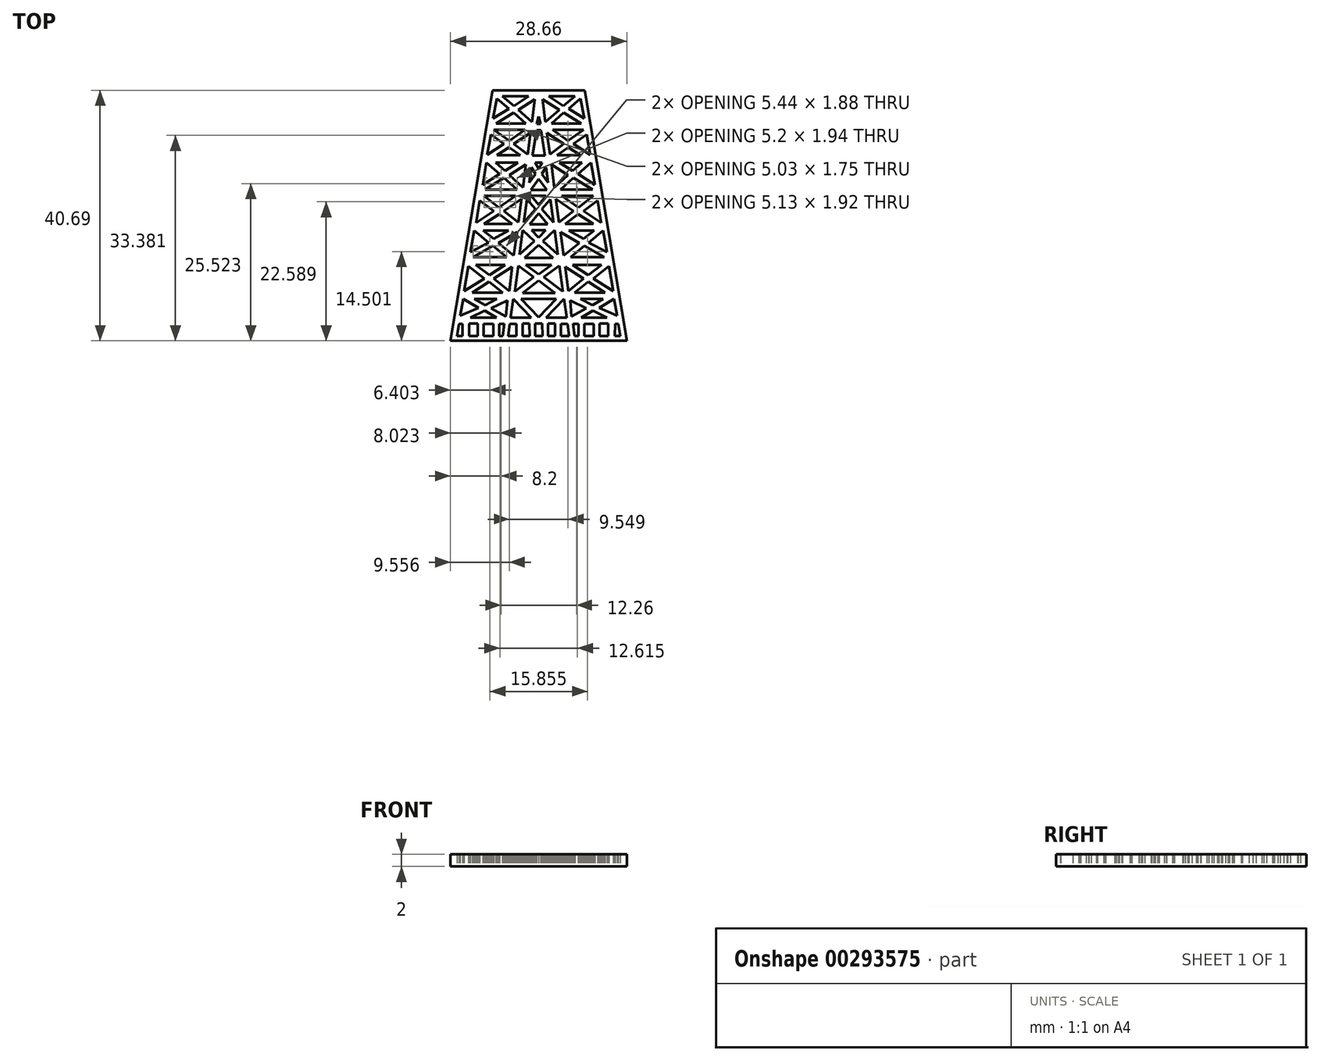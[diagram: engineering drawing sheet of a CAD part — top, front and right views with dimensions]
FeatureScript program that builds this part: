
annotation { "Feature Type Name" : "Feature", "Feature Type Description" : "" }
export const myFeature = defineFeature(function(context is Context, id is Id, definition is map)
    precondition{}
    {
        {
            var Q0;
            Q0=qCreatedBy(makeId("Top.planeOp"),FACE);
            var sketch = newSketch(context, id + "F0", { "sketchPlane" : qUnion([Q0])});
            skLineSegment(sketch, "E0", {"start": v(0, 19.4) * mm, "end": v(-7.5, 19.4) * mm});
            skLineSegment(sketch, "E1", {"start": v(-7.5, 19.4) * mm, "end": v(-14.33, -21.3) * mm});
            skLineSegment(sketch, "E2", {"start": v(-14.33, -21.3) * mm, "end": v(0, -21.3) * mm});
            skLineSegment(sketch, "E3", {"start": v(-1.53, -18.52) * mm, "end": v(-2.64, -18.52) * mm});
            skLineSegment(sketch, "E4", {"start": v(-2.64, -18.52) * mm, "end": v(-2.64, -20.5) * mm});
            skLineSegment(sketch, "E5", {"start": v(-2.64, -20.5) * mm, "end": v(-1.5, -20.5) * mm});
            skLineSegment(sketch, "E6", {"start": v(-1.5, -20.5) * mm, "end": v(-1.53, -18.52) * mm});
            skLineSegment(sketch, "E7", {"start": v(-4.7, -18.55) * mm, "end": v(-3.64, -18.55) * mm});
            skLineSegment(sketch, "E8", {"start": v(-3.64, -18.55) * mm, "end": v(-3.64, -20.51) * mm});
            skLineSegment(sketch, "E9", {"start": v(-3.64, -20.51) * mm, "end": v(-4.95, -20.51) * mm});
            skLineSegment(sketch, "E10", {"start": v(-4.95, -20.51) * mm, "end": v(-4.7, -18.55) * mm});
            skLineSegment(sketch, "E11", {"start": v(-5.57, -18.55) * mm, "end": v(-6.45, -18.55) * mm});
            skLineSegment(sketch, "E12", {"start": v(-6.45, -18.55) * mm, "end": v(-6.45, -20.51) * mm});
            skLineSegment(sketch, "E13", {"start": v(-6.45, -20.51) * mm, "end": v(-5.82, -20.51) * mm});
            skLineSegment(sketch, "E14", {"start": v(-5.82, -20.51) * mm, "end": v(-5.57, -18.55) * mm});
            skLineSegment(sketch, "E15", {"start": v(-8.95, -18.55) * mm, "end": v(-7.4, -18.55) * mm});
            skLineSegment(sketch, "E16", {"start": v(-7.4, -18.55) * mm, "end": v(-7.4, -20.53) * mm});
            skLineSegment(sketch, "E17", {"start": v(-7.4, -20.53) * mm, "end": v(-8.96, -20.53) * mm});
            skLineSegment(sketch, "E18", {"start": v(-8.96, -20.53) * mm, "end": v(-8.95, -18.55) * mm});
            skLineSegment(sketch, "E19", {"start": v(-11.3, -18.55) * mm, "end": v(-11.31, -20.52) * mm});
            skLineSegment(sketch, "E20", {"start": v(-11.31, -20.52) * mm, "end": v(-9.9, -20.52) * mm});
            skLineSegment(sketch, "E21", {"start": v(-9.9, -20.52) * mm, "end": v(-9.9, -18.52) * mm});
            skLineSegment(sketch, "E22", {"start": v(-9.9, -18.52) * mm, "end": v(-11.3, -18.51) * mm});
            skLineSegment(sketch, "E23", {"start": v(-11.3, -18.51) * mm, "end": v(-11.3, -18.55) * mm});
            skLineSegment(sketch, "E24", {"start": v(-12.42, -18.55) * mm, "end": v(-12.97, -18.55) * mm});
            skLineSegment(sketch, "E25", {"start": v(-12.97, -18.55) * mm, "end": v(-13.28, -20.51) * mm});
            skLineSegment(sketch, "E26", {"start": v(-13.28, -20.51) * mm, "end": v(-12.4, -20.52) * mm});
            skLineSegment(sketch, "E27", {"start": v(-12.4, -20.52) * mm, "end": v(-12.42, -18.55) * mm});
            skLineSegment(sketch, "E28", {"start": v(0, -18.51) * mm, "end": v(-0.6, -18.51) * mm});
            skLineSegment(sketch, "E29", {"start": v(-0.6, -18.51) * mm, "end": v(-0.6, -20.55) * mm});
            skLineSegment(sketch, "E30", {"start": v(-0.6, -20.55) * mm, "end": v(0, -20.55) * mm});
            skLineSegment(sketch, "E31", {"start": v(-11.1, -17.58) * mm, "end": v(-6.9, -17.58) * mm});
            skLineSegment(sketch, "E32", {"start": v(-6.9, -17.58) * mm, "end": v(-8.8, -16.38) * mm});
            skLineSegment(sketch, "E33", {"start": v(-8.8, -16.38) * mm, "end": v(-11.1, -17.58) * mm});
            skLineSegment(sketch, "E34", {"start": v(-12.75, -17.25) * mm, "end": v(-9.82, -15.94) * mm});
            skLineSegment(sketch, "E35", {"start": v(-9.82, -15.94) * mm, "end": v(-12.23, -14.52) * mm});
            skLineSegment(sketch, "E36", {"start": v(-12.23, -14.52) * mm, "end": v(-12.75, -17.25) * mm});
            skLineSegment(sketch, "E37", {"start": v(-10.46, -14.51) * mm, "end": v(-6.77, -14.51) * mm});
            skLineSegment(sketch, "E38", {"start": v(-6.77, -14.51) * mm, "end": v(-8.73, -15.53) * mm});
            skLineSegment(sketch, "E39", {"start": v(-8.73, -15.53) * mm, "end": v(-10.46, -14.51) * mm});
            skLineSegment(sketch, "E40", {"start": v(-5.11, -14.74) * mm, "end": v(-5.35, -17.34) * mm});
            skLineSegment(sketch, "E41", {"start": v(-5.35, -17.34) * mm, "end": v(-7.75, -16) * mm});
            skLineSegment(sketch, "E42", {"start": v(-7.75, -16) * mm, "end": v(-5.11, -14.74) * mm});
            skLineSegment(sketch, "E43", {"start": v(-10.8, -13.46) * mm, "end": v(-5.82, -13.46) * mm});
            skLineSegment(sketch, "E44", {"start": v(-5.82, -13.46) * mm, "end": v(-8.08, -11.74) * mm});
            skLineSegment(sketch, "E45", {"start": v(-8.08, -11.74) * mm, "end": v(-10.8, -13.46) * mm});
            skLineSegment(sketch, "E46", {"start": v(-12.11, -13.2) * mm, "end": v(-11.44, -9.16) * mm});
            skLineSegment(sketch, "E47", {"start": v(-11.44, -9.16) * mm, "end": v(-8.86, -11.18) * mm});
            skLineSegment(sketch, "E48", {"start": v(-8.86, -11.18) * mm, "end": v(-12.11, -13.2) * mm});
            skLineSegment(sketch, "E49", {"start": v(-4.33, -9.27) * mm, "end": v(-4.8, -13.2) * mm});
            skLineSegment(sketch, "E50", {"start": v(-4.8, -13.2) * mm, "end": v(-7.3, -11.2) * mm});
            skLineSegment(sketch, "E51", {"start": v(-7.3, -11.2) * mm, "end": v(-4.33, -9.27) * mm});
            skLineSegment(sketch, "E52", {"start": v(-5.5, -8.97) * mm, "end": v(-10.2, -8.97) * mm});
            skLineSegment(sketch, "E53", {"start": v(-10.2, -8.97) * mm, "end": v(-8.02, -10.63) * mm});
            skLineSegment(sketch, "E54", {"start": v(-8.02, -10.63) * mm, "end": v(-5.5, -8.97) * mm});
            skLineSegment(sketch, "E55", {"start": v(-6.57, -5.41) * mm, "end": v(-3.53, -3.67) * mm});
            skLineSegment(sketch, "E56", {"start": v(-3.53, -3.67) * mm, "end": v(-4.08, -7.44) * mm});
            skLineSegment(sketch, "E57", {"start": v(-4.08, -7.44) * mm, "end": v(-6.57, -5.41) * mm});
            skLineSegment(sketch, "E58", {"start": v(-7.4, -5.85) * mm, "end": v(-10.65, -7.73) * mm});
            skLineSegment(sketch, "E59", {"start": v(-10.65, -7.73) * mm, "end": v(-5.2, -7.73) * mm});
            skLineSegment(sketch, "E60", {"start": v(-5.2, -7.73) * mm, "end": v(-7.4, -5.85) * mm});
            skLineSegment(sketch, "E61", {"start": v(-11.1, -6.87) * mm, "end": v(-8.13, -5.33) * mm});
            skLineSegment(sketch, "E62", {"start": v(-8.13, -5.33) * mm, "end": v(-10.46, -3.38) * mm});
            skLineSegment(sketch, "E63", {"start": v(-10.46, -3.38) * mm, "end": v(-11.1, -6.87) * mm});
            skLineSegment(sketch, "E64", {"start": v(-9.03, -3.37) * mm, "end": v(-4.9, -3.37) * mm});
            skLineSegment(sketch, "E65", {"start": v(-4.9, -3.37) * mm, "end": v(-7.3, -4.75) * mm});
            skLineSegment(sketch, "E66", {"start": v(-7.3, -4.75) * mm, "end": v(-9.03, -3.37) * mm});
            skLineSegment(sketch, "E67", {"start": v(-8.87, -2.32) * mm, "end": v(-4.33, -2.32) * mm});
            skLineSegment(sketch, "E68", {"start": v(-4.33, -2.32) * mm, "end": v(-6.43, -0.7) * mm});
            skLineSegment(sketch, "E69", {"start": v(-6.43, -0.7) * mm, "end": v(-8.87, -2.32) * mm});
            skLineSegment(sketch, "E70", {"start": v(-10.17, -2.1) * mm, "end": v(-7.3, -0.22) * mm});
            skLineSegment(sketch, "E71", {"start": v(-7.3, -0.22) * mm, "end": v(-9.57, 1.52) * mm});
            skLineSegment(sketch, "E72", {"start": v(-9.57, 1.52) * mm, "end": v(-10.17, -2.1) * mm});
            skLineSegment(sketch, "E73", {"start": v(-8.87, 2.26) * mm, "end": v(-3.74, 2.26) * mm});
            skLineSegment(sketch, "E74", {"start": v(-3.74, 2.26) * mm, "end": v(-6.47, 0.34) * mm});
            skLineSegment(sketch, "E75", {"start": v(-6.47, 0.34) * mm, "end": v(-8.87, 2.26) * mm});
            skLineSegment(sketch, "E76", {"start": v(-2.8, 1.77) * mm, "end": v(-5.67, -0.23) * mm});
            skLineSegment(sketch, "E77", {"start": v(-5.67, -0.23) * mm, "end": v(-3.3, -2.04) * mm});
            skLineSegment(sketch, "E78", {"start": v(-3.3, -2.04) * mm, "end": v(-2.8, 1.77) * mm});
            skLineSegment(sketch, "E79", {"start": v(-7.02, 7.64) * mm, "end": v(-3.37, 7.64) * mm});
            skLineSegment(sketch, "E80", {"start": v(-3.37, 7.64) * mm, "end": v(-5.5, 6.31) * mm});
            skLineSegment(sketch, "E81", {"start": v(-5.5, 6.31) * mm, "end": v(-7.02, 7.64) * mm});
            skLineSegment(sketch, "E82", {"start": v(-8.5, 7.64) * mm, "end": v(-9.1, 4.06) * mm});
            skLineSegment(sketch, "E83", {"start": v(-9.1, 4.06) * mm, "end": v(-6.38, 5.79) * mm});
            skLineSegment(sketch, "E84", {"start": v(-6.38, 5.79) * mm, "end": v(-8.5, 7.64) * mm});
            skLineSegment(sketch, "E85", {"start": v(-5.67, 5.2) * mm, "end": v(-8.73, 3.26) * mm});
            skLineSegment(sketch, "E86", {"start": v(-8.73, 3.26) * mm, "end": v(-3.53, 3.26) * mm});
            skLineSegment(sketch, "E87", {"start": v(-3.53, 3.26) * mm, "end": v(-5.67, 5.2) * mm});
            skLineSegment(sketch, "E88", {"start": v(-2.07, 7.36) * mm, "end": v(-4.74, 5.62) * mm});
            skLineSegment(sketch, "E89", {"start": v(-4.74, 5.62) * mm, "end": v(-2.56, 3.58) * mm});
            skLineSegment(sketch, "E90", {"start": v(-2.56, 3.58) * mm, "end": v(-2.07, 7.36) * mm});
            skLineSegment(sketch, "E91", {"start": v(-4.08, 10.7) * mm, "end": v(-1.33, 12.5) * mm});
            skLineSegment(sketch, "E92", {"start": v(-1.33, 12.5) * mm, "end": v(-1.8, 9) * mm});
            skLineSegment(sketch, "E93", {"start": v(-1.8, 9) * mm, "end": v(-4.08, 10.7) * mm});
            skLineSegment(sketch, "E94", {"start": v(-2.97, 8.85) * mm, "end": v(-6.77, 8.85) * mm});
            skLineSegment(sketch, "E95", {"start": v(-6.77, 8.85) * mm, "end": v(-4.82, 10.13) * mm});
            skLineSegment(sketch, "E96", {"start": v(-4.82, 10.13) * mm, "end": v(-2.97, 8.85) * mm});
            skLineSegment(sketch, "E97", {"start": v(-8.38, 8.93) * mm, "end": v(-5.65, 10.7) * mm});
            skLineSegment(sketch, "E98", {"start": v(-5.65, 10.7) * mm, "end": v(-7.77, 12.22) * mm});
            skLineSegment(sketch, "E99", {"start": v(-7.77, 12.22) * mm, "end": v(-8.38, 8.93) * mm});
            skLineSegment(sketch, "E100", {"start": v(-7.3, 12.96) * mm, "end": v(-2.26, 12.96) * mm});
            skLineSegment(sketch, "E101", {"start": v(-2.26, 12.96) * mm, "end": v(-4.77, 11.22) * mm});
            skLineSegment(sketch, "E102", {"start": v(-4.77, 11.22) * mm, "end": v(-7.3, 12.96) * mm});
            skLineSegment(sketch, "E103", {"start": v(-6.9, 14) * mm, "end": v(-2.07, 14) * mm});
            skLineSegment(sketch, "E104", {"start": v(-2.07, 14) * mm, "end": v(-4.08, 15.77) * mm});
            skLineSegment(sketch, "E105", {"start": v(-4.08, 15.77) * mm, "end": v(-6.9, 14) * mm});
            skLineSegment(sketch, "E106", {"start": v(-0.62, 17.97) * mm, "end": v(-3.34, 16.25) * mm});
            skLineSegment(sketch, "E107", {"start": v(-3.34, 16.25) * mm, "end": v(-1.07, 14.24) * mm});
            skLineSegment(sketch, "E108", {"start": v(-1.07, 14.24) * mm, "end": v(-0.62, 17.97) * mm});
            skLineSegment(sketch, "E109", {"start": v(-7.4, 14.82) * mm, "end": v(-4.87, 16.4) * mm});
            skLineSegment(sketch, "E110", {"start": v(-4.87, 16.4) * mm, "end": v(-6.77, 18.08) * mm});
            skLineSegment(sketch, "E111", {"start": v(-6.77, 18.08) * mm, "end": v(-7.4, 14.82) * mm});
            skLineSegment(sketch, "E112", {"start": v(-5.89, 18.46) * mm, "end": v(-1.64, 18.46) * mm});
            skLineSegment(sketch, "E113", {"start": v(-1.64, 18.46) * mm, "end": v(-4.02, 16.86) * mm});
            skLineSegment(sketch, "E114", {"start": v(-4.02, 16.86) * mm, "end": v(-5.89, 18.46) * mm});
            skLineSegment(sketch, "E115", {"start": v(0, 13.92) * mm, "end": v(-0.32, 13.92) * mm});
            skLineSegment(sketch, "E116", {"start": v(-0.32, 13.92) * mm, "end": v(0, 15.18) * mm});
            skLineSegment(sketch, "E117", {"start": v(0, 8.8) * mm, "end": v(-1, 8.8) * mm});
            skLineSegment(sketch, "E118", {"start": v(-1, 8.8) * mm, "end": v(-0.35, 12.95) * mm});
            skLineSegment(sketch, "E119", {"start": v(-0.35, 12.95) * mm, "end": v(0, 12.95) * mm});
            skLineSegment(sketch, "E120", {"start": v(0, 7.67) * mm, "end": v(-0.59, 7.67) * mm});
            skLineSegment(sketch, "E121", {"start": v(-0.59, 7.67) * mm, "end": v(0, 6.67) * mm});
            skLineSegment(sketch, "E122", {"start": v(-1.2, 6.9) * mm, "end": v(-1.51, 4.4) * mm});
            skLineSegment(sketch, "E123", {"start": v(-1.51, 4.4) * mm, "end": v(-0.52, 5.8) * mm});
            skLineSegment(sketch, "E124", {"start": v(-0.52, 5.8) * mm, "end": v(-1.2, 6.9) * mm});
            skLineSegment(sketch, "E125", {"start": v(0, 4.98) * mm, "end": v(-1.3, 3.21) * mm});
            skLineSegment(sketch, "E126", {"start": v(-1.3, 3.21) * mm, "end": v(0, 3.21) * mm});
            skLineSegment(sketch, "E127", {"start": v(0, 2.24) * mm, "end": v(-1.2, 2.24) * mm});
            skLineSegment(sketch, "E128", {"start": v(-1.2, 2.24) * mm, "end": v(0, 0.82) * mm});
            skLineSegment(sketch, "E129", {"start": v(-0.53, 0.13) * mm, "end": v(-1.9, 1.67) * mm});
            skLineSegment(sketch, "E130", {"start": v(-1.9, 1.67) * mm, "end": v(-2.4, -2.03) * mm});
            skLineSegment(sketch, "E131", {"start": v(-2.4, -2.03) * mm, "end": v(-0.53, 0.13) * mm});
            skLineSegment(sketch, "E132", {"start": v(0, -0.58) * mm, "end": v(-1.48, -2.37) * mm});
            skLineSegment(sketch, "E133", {"start": v(-1.48, -2.37) * mm, "end": v(0, -2.37) * mm});
            skLineSegment(sketch, "E134", {"start": v(0, -3.33) * mm, "end": v(-1.15, -3.33) * mm});
            skLineSegment(sketch, "E135", {"start": v(-1.15, -3.33) * mm, "end": v(0, -4.54) * mm});
            skLineSegment(sketch, "E136", {"start": v(-0.69, -5.13) * mm, "end": v(-2.6, -3.31) * mm});
            skLineSegment(sketch, "E137", {"start": v(-2.6, -3.31) * mm, "end": v(-3.1, -7.25) * mm});
            skLineSegment(sketch, "E138", {"start": v(-3.1, -7.25) * mm, "end": v(-0.69, -5.13) * mm});
            skLineSegment(sketch, "E139", {"start": v(0, -5.74) * mm, "end": v(-2.32, -7.8) * mm});
            skLineSegment(sketch, "E140", {"start": v(-2.32, -7.8) * mm, "end": v(0, -7.8) * mm});
            skLineSegment(sketch, "E141", {"start": v(-3.33, -9.1) * mm, "end": v(-3.9, -13.33) * mm});
            skLineSegment(sketch, "E142", {"start": v(-3.9, -13.33) * mm, "end": v(-0.81, -10.96) * mm});
            skLineSegment(sketch, "E143", {"start": v(-0.81, -10.96) * mm, "end": v(-3.33, -9.1) * mm});
            skLineSegment(sketch, "E144", {"start": v(-4.13, -14.53) * mm, "end": v(-4.55, -17.57) * mm});
            skLineSegment(sketch, "E145", {"start": v(-4.55, -17.57) * mm, "end": v(-1.19, -17.57) * mm});
            skLineSegment(sketch, "E146", {"start": v(-1.19, -17.57) * mm, "end": v(-4.13, -14.53) * mm});
            skLineSegment(sketch, "E147", {"start": v(0, -14.53) * mm, "end": v(-2.87, -14.53) * mm});
            skLineSegment(sketch, "E148", {"start": v(-2.87, -14.53) * mm, "end": v(0, -17.46) * mm});
            skLineSegment(sketch, "E149", {"start": v(0, -13.53) * mm, "end": v(-2.63, -13.53) * mm});
            skLineSegment(sketch, "E150", {"start": v(-2.63, -13.53) * mm, "end": v(0, -11.52) * mm});
            skLineSegment(sketch, "E151", {"start": v(0, -10.47) * mm, "end": v(-2.09, -8.97) * mm});
            skLineSegment(sketch, "E152", {"start": v(-2.09, -8.97) * mm, "end": v(0, -8.97) * mm});
            skLineSegment(sketch, "E153.MirrorCS", {"start": v(5.89, 18.46) * mm, "end": v(1.64, 18.46) * mm});
            skLineSegment(sketch, "E154.MirrorCS", {"start": v(4.02, 16.86) * mm, "end": v(5.89, 18.46) * mm});
            skLineSegment(sketch, "E155.MirrorCS", {"start": v(1.64, 18.46) * mm, "end": v(4.02, 16.86) * mm});
            skLineSegment(sketch, "E156.MirrorCS", {"start": v(0.62, 17.97) * mm, "end": v(3.34, 16.25) * mm});
            skLineSegment(sketch, "E157.MirrorCS", {"start": v(1.07, 14.24) * mm, "end": v(0.62, 17.97) * mm});
            skLineSegment(sketch, "E158.MirrorCS", {"start": v(3.34, 16.25) * mm, "end": v(1.07, 14.24) * mm});
            skLineSegment(sketch, "E159.MirrorCS", {"start": v(2.07, 14) * mm, "end": v(4.08, 15.77) * mm});
            skLineSegment(sketch, "E160.MirrorCS", {"start": v(6.9, 14) * mm, "end": v(2.07, 14) * mm});
            skLineSegment(sketch, "E161.MirrorCS", {"start": v(4.08, 15.77) * mm, "end": v(6.9, 14) * mm});
            skLineSegment(sketch, "E162.MirrorCS", {"start": v(7.4, 14.82) * mm, "end": v(4.87, 16.4) * mm});
            skLineSegment(sketch, "E163.MirrorCS", {"start": v(6.77, 18.08) * mm, "end": v(7.4, 14.82) * mm});
            skLineSegment(sketch, "E164.MirrorCS", {"start": v(7.3, 12.96) * mm, "end": v(2.26, 12.96) * mm});
            skLineSegment(sketch, "E165.MirrorCS", {"start": v(4.77, 11.22) * mm, "end": v(7.3, 12.96) * mm});
            skLineSegment(sketch, "E166.MirrorCS", {"start": v(5.65, 10.7) * mm, "end": v(7.77, 12.22) * mm});
            skLineSegment(sketch, "E167.MirrorCS", {"start": v(7.77, 12.22) * mm, "end": v(8.38, 8.93) * mm});
            skLineSegment(sketch, "E168.MirrorCS", {"start": v(8.38, 8.93) * mm, "end": v(5.65, 10.7) * mm});
            skLineSegment(sketch, "E169.MirrorCS", {"start": v(6.77, 8.85) * mm, "end": v(4.82, 10.13) * mm});
            skLineSegment(sketch, "E170.MirrorCS", {"start": v(2.97, 8.85) * mm, "end": v(6.77, 8.85) * mm});
            skLineSegment(sketch, "E171.MirrorCS", {"start": v(4.82, 10.13) * mm, "end": v(2.97, 8.85) * mm});
            skLineSegment(sketch, "E172.MirrorCS", {"start": v(1.8, 9) * mm, "end": v(4.08, 10.7) * mm});
            skLineSegment(sketch, "E173.MirrorCS", {"start": v(1.33, 12.5) * mm, "end": v(1.8, 9) * mm});
            skLineSegment(sketch, "E174.MirrorCS", {"start": v(4.08, 10.7) * mm, "end": v(1.33, 12.5) * mm});
            skLineSegment(sketch, "E175.MirrorCS", {"start": v(2.26, 12.96) * mm, "end": v(4.77, 11.22) * mm});
            skLineSegment(sketch, "E176.MirrorCS", {"start": v(7.02, 7.64) * mm, "end": v(3.37, 7.64) * mm});
            skLineSegment(sketch, "E177.MirrorCS", {"start": v(5.5, 6.31) * mm, "end": v(7.02, 7.64) * mm});
            skLineSegment(sketch, "E178.MirrorCS", {"start": v(6.38, 5.79) * mm, "end": v(8.5, 7.64) * mm});
            skLineSegment(sketch, "E179.MirrorCS", {"start": v(8.5, 7.64) * mm, "end": v(9.1, 4.06) * mm});
            skLineSegment(sketch, "E180.MirrorCS", {"start": v(9.1, 4.06) * mm, "end": v(6.38, 5.79) * mm});
            skLineSegment(sketch, "E181.MirrorCS", {"start": v(5.67, 5.2) * mm, "end": v(8.73, 3.26) * mm});
            skLineSegment(sketch, "E182.MirrorCS", {"start": v(3.53, 3.26) * mm, "end": v(5.67, 5.2) * mm});
            skLineSegment(sketch, "E183.MirrorCS", {"start": v(4.74, 5.62) * mm, "end": v(2.56, 3.58) * mm});
            skLineSegment(sketch, "E184.MirrorCS", {"start": v(8.73, 3.26) * mm, "end": v(3.53, 3.26) * mm});
            skLineSegment(sketch, "E185.MirrorCS", {"start": v(2.56, 3.58) * mm, "end": v(2.07, 7.36) * mm});
            skLineSegment(sketch, "E186.MirrorCS", {"start": v(2.07, 7.36) * mm, "end": v(4.74, 5.62) * mm});
            skLineSegment(sketch, "E187.MirrorCS", {"start": v(3.37, 7.64) * mm, "end": v(5.5, 6.31) * mm});
            skLineSegment(sketch, "E188.MirrorCS", {"start": v(3.74, 2.26) * mm, "end": v(6.47, 0.34) * mm});
            skLineSegment(sketch, "E189.MirrorCS", {"start": v(8.87, 2.26) * mm, "end": v(3.74, 2.26) * mm});
            skLineSegment(sketch, "E190.MirrorCS", {"start": v(6.47, 0.34) * mm, "end": v(8.87, 2.26) * mm});
            skLineSegment(sketch, "E191.MirrorCS", {"start": v(7.3, -0.22) * mm, "end": v(9.57, 1.52) * mm});
            skLineSegment(sketch, "E192.MirrorCS", {"start": v(9.57, 1.52) * mm, "end": v(10.17, -2.1) * mm});
            skLineSegment(sketch, "E193.MirrorCS", {"start": v(10.17, -2.1) * mm, "end": v(7.3, -0.22) * mm});
            skLineSegment(sketch, "E194.MirrorCS", {"start": v(6.43, -0.7) * mm, "end": v(8.87, -2.32) * mm});
            skLineSegment(sketch, "E195.MirrorCS", {"start": v(8.87, -2.32) * mm, "end": v(4.33, -2.32) * mm});
            skLineSegment(sketch, "E196.MirrorCS", {"start": v(4.33, -2.32) * mm, "end": v(6.43, -0.7) * mm});
            skLineSegment(sketch, "E197.MirrorCS", {"start": v(5.67, -0.23) * mm, "end": v(3.3, -2.04) * mm});
            skLineSegment(sketch, "E198.MirrorCS", {"start": v(3.3, -2.04) * mm, "end": v(2.8, 1.77) * mm});
            skLineSegment(sketch, "E199.MirrorCS", {"start": v(2.8, 1.77) * mm, "end": v(5.67, -0.23) * mm});
            skLineSegment(sketch, "E200.MirrorCS", {"start": v(9.03, -3.37) * mm, "end": v(4.9, -3.37) * mm});
            skLineSegment(sketch, "E201.MirrorCS", {"start": v(7.3, -4.75) * mm, "end": v(9.03, -3.37) * mm});
            skLineSegment(sketch, "E202.MirrorCS", {"start": v(8.13, -5.33) * mm, "end": v(10.46, -3.38) * mm});
            skLineSegment(sketch, "E203.MirrorCS", {"start": v(10.46, -3.38) * mm, "end": v(11.1, -6.87) * mm});
            skLineSegment(sketch, "E204.MirrorCS", {"start": v(11.1, -6.87) * mm, "end": v(8.13, -5.33) * mm});
            skLineSegment(sketch, "E205.MirrorCS", {"start": v(7.4, -5.85) * mm, "end": v(10.65, -7.73) * mm});
            skLineSegment(sketch, "E206.MirrorCS", {"start": v(10.65, -7.73) * mm, "end": v(5.2, -7.73) * mm});
            skLineSegment(sketch, "E207.MirrorCS", {"start": v(5.2, -7.73) * mm, "end": v(7.4, -5.85) * mm});
            skLineSegment(sketch, "E208.MirrorCS", {"start": v(4.08, -7.44) * mm, "end": v(6.57, -5.41) * mm});
            skLineSegment(sketch, "E209.MirrorCS", {"start": v(3.53, -3.67) * mm, "end": v(4.08, -7.44) * mm});
            skLineSegment(sketch, "E210.MirrorCS", {"start": v(6.57, -5.41) * mm, "end": v(3.53, -3.67) * mm});
            skLineSegment(sketch, "E211.MirrorCS", {"start": v(7.3, -11.2) * mm, "end": v(4.33, -9.27) * mm});
            skLineSegment(sketch, "E212.MirrorCS", {"start": v(8.02, -10.63) * mm, "end": v(5.5, -8.97) * mm});
            skLineSegment(sketch, "E213.MirrorCS", {"start": v(5.5, -8.97) * mm, "end": v(10.2, -8.97) * mm});
            skLineSegment(sketch, "E214.MirrorCS", {"start": v(10.2, -8.97) * mm, "end": v(8.02, -10.63) * mm});
            skLineSegment(sketch, "E215.MirrorCS", {"start": v(11.44, -9.16) * mm, "end": v(8.86, -11.18) * mm});
            skLineSegment(sketch, "E216.MirrorCS", {"start": v(12.11, -13.2) * mm, "end": v(11.44, -9.16) * mm});
            skLineSegment(sketch, "E217.MirrorCS", {"start": v(8.86, -11.18) * mm, "end": v(12.11, -13.2) * mm});
            skLineSegment(sketch, "E218.MirrorCS", {"start": v(8.08, -11.74) * mm, "end": v(10.8, -13.46) * mm});
            skLineSegment(sketch, "E219.MirrorCS", {"start": v(10.8, -13.46) * mm, "end": v(5.82, -13.46) * mm});
            skLineSegment(sketch, "E220.MirrorCS", {"start": v(5.82, -13.46) * mm, "end": v(8.08, -11.74) * mm});
            skLineSegment(sketch, "E221.MirrorCS", {"start": v(4.8, -13.2) * mm, "end": v(7.3, -11.2) * mm});
            skLineSegment(sketch, "E222.MirrorCS", {"start": v(4.33, -9.27) * mm, "end": v(4.8, -13.2) * mm});
            skLineSegment(sketch, "E223.MirrorCS", {"start": v(11.1, -17.58) * mm, "end": v(6.9, -17.58) * mm});
            skLineSegment(sketch, "E224.MirrorCS", {"start": v(6.9, -17.58) * mm, "end": v(8.8, -16.38) * mm});
            skLineSegment(sketch, "E225.MirrorCS", {"start": v(8.8, -16.38) * mm, "end": v(11.1, -17.58) * mm});
            skLineSegment(sketch, "E226.MirrorCS", {"start": v(12.75, -17.25) * mm, "end": v(9.82, -15.94) * mm});
            skLineSegment(sketch, "E227.MirrorCS", {"start": v(12.23, -14.52) * mm, "end": v(12.75, -17.25) * mm});
            skLineSegment(sketch, "E228.MirrorCS", {"start": v(9.82, -15.94) * mm, "end": v(12.23, -14.52) * mm});
            skLineSegment(sketch, "E229.MirrorCS", {"start": v(8.73, -15.53) * mm, "end": v(10.46, -14.51) * mm});
            skLineSegment(sketch, "E230.MirrorCS", {"start": v(10.46, -14.51) * mm, "end": v(6.77, -14.51) * mm});
            skLineSegment(sketch, "E231.MirrorCS", {"start": v(6.77, -14.51) * mm, "end": v(8.73, -15.53) * mm});
            skLineSegment(sketch, "E232.MirrorCS", {"start": v(7.75, -16) * mm, "end": v(5.11, -14.74) * mm});
            skLineSegment(sketch, "E233.MirrorCS", {"start": v(5.11, -14.74) * mm, "end": v(5.35, -17.34) * mm});
            skLineSegment(sketch, "E234.MirrorCS", {"start": v(5.35, -17.34) * mm, "end": v(7.75, -16) * mm});
            skLineSegment(sketch, "E235.MirrorCS", {"start": v(4.55, -17.57) * mm, "end": v(1.19, -17.57) * mm});
            skLineSegment(sketch, "E236.MirrorCS", {"start": v(4.13, -14.53) * mm, "end": v(4.55, -17.57) * mm});
            skLineSegment(sketch, "E237.MirrorCS", {"start": v(1.19, -17.57) * mm, "end": v(4.13, -14.53) * mm});
            skLineSegment(sketch, "E238.MirrorCS", {"start": v(0, -14.53) * mm, "end": v(2.87, -14.53) * mm});
            skLineSegment(sketch, "E239.MirrorCS", {"start": v(2.87, -14.53) * mm, "end": v(0, -17.46) * mm});
            skLineSegment(sketch, "E240.MirrorCS", {"start": v(0, -13.53) * mm, "end": v(2.63, -13.53) * mm});
            skLineSegment(sketch, "E241.MirrorCS", {"start": v(2.63, -13.53) * mm, "end": v(0, -11.52) * mm});
            skLineSegment(sketch, "E242.MirrorCS", {"start": v(3.9, -13.33) * mm, "end": v(0.81, -10.96) * mm});
            skLineSegment(sketch, "E243.MirrorCS", {"start": v(3.33, -9.1) * mm, "end": v(3.9, -13.33) * mm});
            skLineSegment(sketch, "E244.MirrorCS", {"start": v(0.81, -10.96) * mm, "end": v(3.33, -9.1) * mm});
            skLineSegment(sketch, "E245.MirrorCS", {"start": v(0, -10.47) * mm, "end": v(2.09, -8.97) * mm});
            skLineSegment(sketch, "E246.MirrorCS", {"start": v(2.09, -8.97) * mm, "end": v(0, -8.97) * mm});
            skLineSegment(sketch, "E247.MirrorCS", {"start": v(2.32, -7.8) * mm, "end": v(0, -7.8) * mm});
            skLineSegment(sketch, "E248.MirrorCS", {"start": v(0, -5.74) * mm, "end": v(2.32, -7.8) * mm});
            skLineSegment(sketch, "E249.MirrorCS", {"start": v(3.1, -7.25) * mm, "end": v(0.69, -5.13) * mm});
            skLineSegment(sketch, "E250.MirrorCS", {"start": v(2.6, -3.31) * mm, "end": v(3.1, -7.25) * mm});
            skLineSegment(sketch, "E251.MirrorCS", {"start": v(0.69, -5.13) * mm, "end": v(2.6, -3.31) * mm});
            skLineSegment(sketch, "E252.MirrorCS", {"start": v(1.15, -3.33) * mm, "end": v(0, -4.54) * mm});
            skLineSegment(sketch, "E253.MirrorCS", {"start": v(0, -3.33) * mm, "end": v(1.15, -3.33) * mm});
            skLineSegment(sketch, "E254.MirrorCS", {"start": v(1.48, -2.37) * mm, "end": v(0, -2.37) * mm});
            skLineSegment(sketch, "E255.MirrorCS", {"start": v(0, -0.58) * mm, "end": v(1.48, -2.37) * mm});
            skLineSegment(sketch, "E256.MirrorCS", {"start": v(2.4, -2.03) * mm, "end": v(0.53, 0.13) * mm});
            skLineSegment(sketch, "E257.MirrorCS", {"start": v(1.9, 1.67) * mm, "end": v(2.4, -2.03) * mm});
            skLineSegment(sketch, "E258.MirrorCS", {"start": v(0.53, 0.13) * mm, "end": v(1.9, 1.67) * mm});
            skLineSegment(sketch, "E259.MirrorCS", {"start": v(0, 2.24) * mm, "end": v(1.2, 2.24) * mm});
            skLineSegment(sketch, "E260.MirrorCS", {"start": v(1.2, 2.24) * mm, "end": v(0, 0.82) * mm});
            skLineSegment(sketch, "E261.MirrorCS", {"start": v(1.3, 3.21) * mm, "end": v(0, 3.21) * mm});
            skLineSegment(sketch, "E262.MirrorCS", {"start": v(0, 4.98) * mm, "end": v(1.3, 3.21) * mm});
            skLineSegment(sketch, "E263.MirrorCS", {"start": v(1.51, 4.4) * mm, "end": v(0.52, 5.8) * mm});
            skLineSegment(sketch, "E264.MirrorCS", {"start": v(1.2, 6.9) * mm, "end": v(1.51, 4.4) * mm});
            skLineSegment(sketch, "E265.MirrorCS", {"start": v(0, 8.8) * mm, "end": v(1, 8.8) * mm});
            skLineSegment(sketch, "E266.MirrorCS", {"start": v(1, 8.8) * mm, "end": v(0.35, 12.95) * mm});
            skLineSegment(sketch, "E267.MirrorCS", {"start": v(0.35, 12.95) * mm, "end": v(0, 12.95) * mm});
            skLineSegment(sketch, "E268.MirrorCS", {"start": v(0, 13.92) * mm, "end": v(0.32, 13.92) * mm});
            skLineSegment(sketch, "E269.MirrorCS", {"start": v(0.32, 13.92) * mm, "end": v(0, 15.18) * mm});
            skLineSegment(sketch, "E270.MirrorCS", {"start": v(0, 7.67) * mm, "end": v(0.59, 7.67) * mm});
            skLineSegment(sketch, "E271.MirrorCS", {"start": v(0.59, 7.67) * mm, "end": v(0, 6.67) * mm});
            skLineSegment(sketch, "E272.MirrorCS", {"start": v(0.52, 5.8) * mm, "end": v(1.2, 6.9) * mm});
            skLineSegment(sketch, "E273.MirrorCS", {"start": v(0, 19.4) * mm, "end": v(7.5, 19.4) * mm});
            skLineSegment(sketch, "E274.MirrorCS", {"start": v(7.5, 19.4) * mm, "end": v(14.33, -21.3) * mm});
            skLineSegment(sketch, "E275.MirrorCS", {"start": v(14.33, -21.3) * mm, "end": v(0, -21.3) * mm});
            skLineSegment(sketch, "E276.MirrorCS", {"start": v(13.28, -20.51) * mm, "end": v(12.4, -20.52) * mm});
            skLineSegment(sketch, "E277.MirrorCS", {"start": v(12.97, -18.55) * mm, "end": v(13.28, -20.51) * mm});
            skLineSegment(sketch, "E278.MirrorCS", {"start": v(12.4, -20.52) * mm, "end": v(12.42, -18.55) * mm});
            skLineSegment(sketch, "E279.MirrorCS", {"start": v(12.42, -18.55) * mm, "end": v(12.97, -18.55) * mm});
            skLineSegment(sketch, "E280.MirrorCS", {"start": v(9.9, -18.52) * mm, "end": v(11.3, -18.51) * mm});
            skLineSegment(sketch, "E281.MirrorCS", {"start": v(11.3, -18.55) * mm, "end": v(11.31, -20.52) * mm});
            skLineSegment(sketch, "E282.MirrorCS", {"start": v(11.31, -20.52) * mm, "end": v(9.9, -20.52) * mm});
            skLineSegment(sketch, "E283.MirrorCS", {"start": v(9.9, -20.52) * mm, "end": v(9.9, -18.52) * mm});
            skLineSegment(sketch, "E284.MirrorCS", {"start": v(8.96, -20.53) * mm, "end": v(8.95, -18.55) * mm});
            skLineSegment(sketch, "E285.MirrorCS", {"start": v(7.4, -20.53) * mm, "end": v(8.96, -20.53) * mm});
            skLineSegment(sketch, "E286.MirrorCS", {"start": v(8.95, -18.55) * mm, "end": v(7.4, -18.55) * mm});
            skLineSegment(sketch, "E287.MirrorCS", {"start": v(7.4, -18.55) * mm, "end": v(7.4, -20.53) * mm});
            skLineSegment(sketch, "E288.MirrorCS", {"start": v(5.57, -18.55) * mm, "end": v(6.45, -18.55) * mm});
            skLineSegment(sketch, "E289.MirrorCS", {"start": v(6.45, -18.55) * mm, "end": v(6.45, -20.51) * mm});
            skLineSegment(sketch, "E290.MirrorCS", {"start": v(6.45, -20.51) * mm, "end": v(5.82, -20.51) * mm});
            skLineSegment(sketch, "E291.MirrorCS", {"start": v(5.82, -20.51) * mm, "end": v(5.57, -18.55) * mm});
            skLineSegment(sketch, "E292.MirrorCS", {"start": v(4.95, -20.51) * mm, "end": v(4.7, -18.55) * mm});
            skLineSegment(sketch, "E293.MirrorCS", {"start": v(3.64, -20.51) * mm, "end": v(4.95, -20.51) * mm});
            skLineSegment(sketch, "E294.MirrorCS", {"start": v(3.64, -18.55) * mm, "end": v(3.64, -20.51) * mm});
            skLineSegment(sketch, "E295.MirrorCS", {"start": v(4.7, -18.55) * mm, "end": v(3.64, -18.55) * mm});
            skLineSegment(sketch, "E296.MirrorCS", {"start": v(1.53, -18.52) * mm, "end": v(2.64, -18.52) * mm});
            skLineSegment(sketch, "E297.MirrorCS", {"start": v(2.64, -18.52) * mm, "end": v(2.64, -20.5) * mm});
            skLineSegment(sketch, "E298.MirrorCS", {"start": v(2.64, -20.5) * mm, "end": v(1.5, -20.5) * mm});
            skLineSegment(sketch, "E299.MirrorCS", {"start": v(1.5, -20.5) * mm, "end": v(1.53, -18.52) * mm});
            skLineSegment(sketch, "E300.MirrorCS", {"start": v(0.6, -20.55) * mm, "end": v(0, -20.55) * mm});
            skLineSegment(sketch, "E301.MirrorCS", {"start": v(0.6, -18.51) * mm, "end": v(0.6, -20.55) * mm});
            skLineSegment(sketch, "E302.MirrorCS", {"start": v(0, -18.51) * mm, "end": v(0.6, -18.51) * mm});
            skLineSegment(sketch, "E303", {"start": v(11.3, -18.55) * mm, "end": v(11.3, -18.51) * mm});
            skLineSegment(sketch, "E304.MirrorCS", {"start": v(4.9, -3.37) * mm, "end": v(7.3, -4.75) * mm});
            skLineSegment(sketch, "E305.MirrorCS", {"start": v(4.87, 16.4) * mm, "end": v(6.77, 18.08) * mm});
            skSolve(sketch);
        }
        {
            var Q0;
            Q0=makeQuery(id+"F0.imprint","IMPRINT",FACE,{"disambiguationData":[TD([[makeQuery(id+"F0.imprint","IMPRINT",EDGE,{"derivedFrom":sQuery(id+"F0.wireOp",EDGE,"E0")}),1.0]])]});
            extrude(context, id + "F1", {"entities" : qUnion([Q0]), "depth" : 2 * mm});
        }
    });
